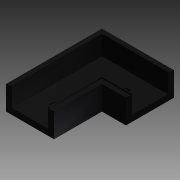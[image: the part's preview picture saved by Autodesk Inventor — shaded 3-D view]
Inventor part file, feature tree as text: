
AUTODESK INVENTOR PART (.ipt)
format: ipt  version: 2015 (Build 190159000, 159)  size: 165,376 bytes
history: native  units: in
note: dims shown in document units (in); Inventor stores cm internally (conversion verified against a paired STEP export)
features: extrude x5, sketch x5, other x2, split x1
ambient origin geometry x8: Origin, YZ Plane, XZ Plane, XY Plane, X Axis, Y Axis, Z Axis, Center Point
bodies: Solid1 (feature_tree)
feature tree (13):
  extrude  "Extrusion1"  Depth=1.0in
  extrude  "Extrusion2"  Depth=0.5in TaperAngle=0.0deg
  extrude  "Extrusion4"  Depth=0.75in
  extrude  "Extrusion5"  Depth=0.75in
  extrude  "Extrusion6"  Depth=0.03in TaperAngle=0.0deg
  split  "Split2"
  other  "Lip4"
  other  "Lip5"
  sketch  "Sketch1"  dims[d0=1.0in d1=1.0in]
  sketch  "Sketch2"  dims[d2=2.0in d3=0.0in d4=0.5in d5=0.0in]
  sketch  "Sketch5"  dims[d8=0.75in d9=0.75in]
  sketch  "Sketch6"  dims[d10=1.75in d11=0.0in d12=0.75in]
  sketch  "Sketch7"  dims[d13=0.75in d14=1.75in d15=0.0in d34=0.141in d35=1.0in d36=0.0in d38=0.03in d39=0.03in d40=0.0in d41=0.0in d42=0.0in d43=0.0in d44=0.03in d45=0.03in d46=0.0in d47=0.0in d48=0.0in d49=0.0in]
